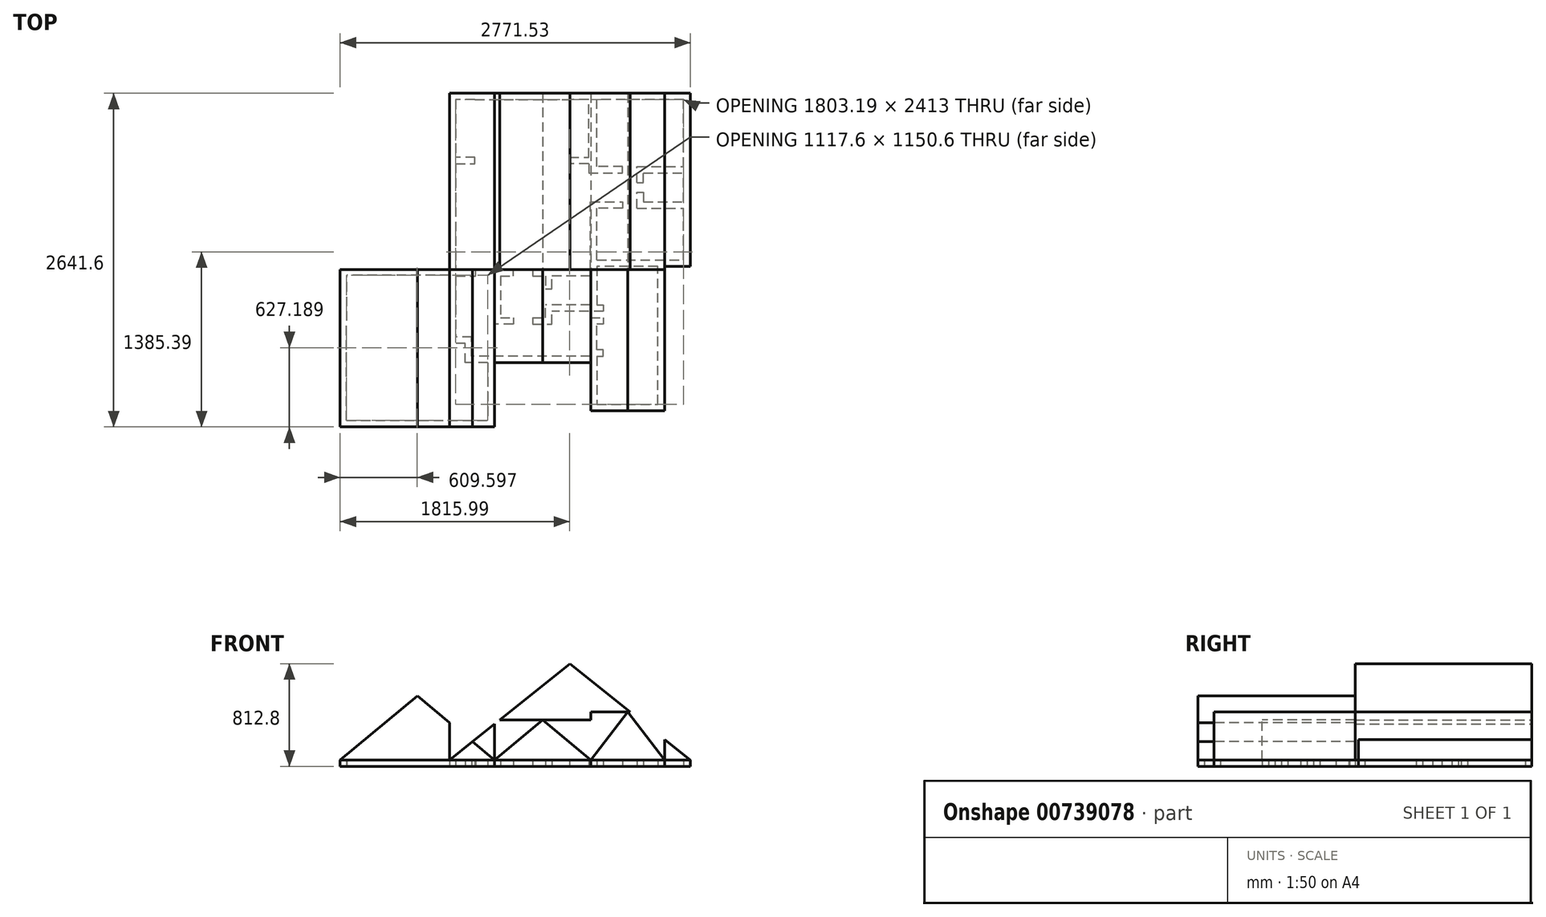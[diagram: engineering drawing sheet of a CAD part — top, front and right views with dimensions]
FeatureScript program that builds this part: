
annotation { "Feature Type Name" : "Feature", "Feature Type Description" : "" }
export const myFeature = defineFeature(function(context is Context, id is Id, definition is map)
    precondition{}
    {
        {
            var Q0;
            Q0=qCreatedBy(makeId("Top.planeOp"),FACE);
            var sketch = newSketch(context, id + "F0", { "sketchPlane" : qUnion([Q0])});
            skLineSegment(sketch, "E0", {"start": v(-1139.86, -1123.82) * mm, "end": v(-606.46, -1123.82) * mm});
            skLineSegment(sketch, "E1", {"start": v(256.93, -615.82) * mm, "end": v(256.93, -996.82) * mm});
            skLineSegment(sketch, "E2", {"start": v(256.93, -996.82) * mm, "end": v(739.53, -996.82) * mm});
            skLineSegment(sketch, "E3", {"start": v(688.73, 146.18) * mm, "end": v(942.73, 146.18) * mm});
            skLineSegment(sketch, "E4", {"start": v(942.73, 1416.18) * mm, "end": v(256.93, 1416.18) * mm});
            skLineSegment(sketch, "E5", {"start": v(-908.33, 26.78) * mm, "end": v(-1441.73, 26.78) * mm});
            skLineSegment(sketch, "E6", {"start": v(-1444.66, 68.9) * mm, "end": v(-962.06, 68.9) * mm});
            skLineSegment(sketch, "E7", {"start": v(-1187.73, -1175.7) * mm, "end": v(-552.73, -1175.7) * mm});
            skLineSegment(sketch, "E8", {"start": v(-552.73, -1175.7) * mm, "end": v(-552.73, -667.7) * mm});
            skLineSegment(sketch, "E9", {"start": v(-552.73, -667.7) * mm, "end": v(209.27, -667.7) * mm});
            skLineSegment(sketch, "E10", {"start": v(209.27, -667.7) * mm, "end": v(209.27, -1048.7) * mm});
            skLineSegment(sketch, "E11", {"start": v(209.27, -1048.7) * mm, "end": v(793.47, -1048.7) * mm});
            skLineSegment(sketch, "E12", {"start": v(996.67, 94.3) * mm, "end": v(996.67, 1465.9) * mm});
            skLineSegment(sketch, "E13", {"start": v(996.67, 1465.9) * mm, "end": v(209.27, 1465.9) * mm});
            skLineSegment(sketch, "E14", {"start": v(-606.46, -667.7) * mm, "end": v(-657.26, -667.7) * mm});
            skLineSegment(sketch, "E15", {"start": v(-657.26, -667.7) * mm, "end": v(-784.26, -667.7) * mm});
            skLineSegment(sketch, "E16", {"start": v(-784.26, -667.7) * mm, "end": v(-784.26, -515.3) * mm});
            skLineSegment(sketch, "E17", {"start": v(-784.26, -515.3) * mm, "end": v(-908.33, -515.3) * mm});
            skLineSegment(sketch, "E18", {"start": v(-908.33, -515.3) * mm, "end": v(-908.33, 26.78) * mm});
            skLineSegment(sketch, "E19", {"start": v(-860.46, 19.18) * mm, "end": v(-860.46, -463.42) * mm});
            skLineSegment(sketch, "E20", {"start": v(-733.46, -615.82) * mm, "end": v(-606.46, -615.82) * mm});
            skLineSegment(sketch, "E21", {"start": v(-962.06, 68.9) * mm, "end": v(-908.33, 68.9) * mm});
            skLineSegment(sketch, "E22", {"start": v(-908.33, 68.9) * mm, "end": v(-908.33, 957.9) * mm});
            skLineSegment(sketch, "E23", {"start": v(-606.46, -667.7) * mm, "end": v(-606.46, -1123.82) * mm});
            skLineSegment(sketch, "E24", {"start": v(688.73, 95.38) * mm, "end": v(256.93, 95.38) * mm});
            skLineSegment(sketch, "E25", {"start": v(793.47, -1048.7) * mm, "end": v(793.47, 94.3) * mm});
            skLineSegment(sketch, "E26", {"start": v(793.47, 94.3) * mm, "end": v(996.67, 94.3) * mm});
            skLineSegment(sketch, "E27", {"start": v(739.53, -996.82) * mm, "end": v(739.53, 95.38) * mm});
            skLineSegment(sketch, "E28", {"start": v(739.53, 95.38) * mm, "end": v(688.73, 95.38) * mm});
            skLineSegment(sketch, "E29", {"start": v(256.93, -615.82) * mm, "end": v(307.73, -615.82) * mm});
            skLineSegment(sketch, "E30", {"start": v(383.93, -615.82) * mm, "end": v(510.93, -615.82) * mm});
            skLineSegment(sketch, "E31", {"start": v(739.53, -615.82) * mm, "end": v(637.93, -615.82) * mm});
            skLineSegment(sketch, "E32", {"start": v(383.93, -615.82) * mm, "end": v(383.93, -526.92) * mm});
            skLineSegment(sketch, "E33", {"start": v(739.53, -312.49) * mm, "end": v(739.53, -374.51) * mm});
            skLineSegment(sketch, "E34", {"start": v(383.93, -209.42) * mm, "end": v(510.93, -209.42) * mm});
            skLineSegment(sketch, "E35", {"start": v(739.53, -209.42) * mm, "end": v(637.93, -209.42) * mm});
            skLineSegment(sketch, "E36", {"start": v(383.93, -526.92) * mm, "end": v(383.93, -473.07) * mm});
            skLineSegment(sketch, "E37", {"start": v(383.93, -312.49) * mm, "end": v(383.93, -366.33) * mm});
            skLineSegment(sketch, "E38", {"start": v(256.93, -158.62) * mm, "end": v(256.93, 95.38) * mm});
            skLineSegment(sketch, "E39", {"start": v(510.93, -209.42) * mm, "end": v(510.93, -234.82) * mm});
            skLineSegment(sketch, "E40", {"start": v(510.93, -234.82) * mm, "end": v(409.33, -234.82) * mm});
            skLineSegment(sketch, "E41", {"start": v(409.33, -234.82) * mm, "end": v(409.33, -285.62) * mm});
            skLineSegment(sketch, "E42", {"start": v(409.33, -285.62) * mm, "end": v(714.13, -285.62) * mm});
            skLineSegment(sketch, "E43", {"start": v(714.13, -285.62) * mm, "end": v(714.13, -234.82) * mm});
            skLineSegment(sketch, "E44", {"start": v(714.13, -234.82) * mm, "end": v(637.93, -234.82) * mm});
            skLineSegment(sketch, "E45", {"start": v(637.93, -234.82) * mm, "end": v(637.93, -209.42) * mm});
            skLineSegment(sketch, "E46", {"start": v(383.93, -366.33) * mm, "end": v(409.33, -366.33) * mm});
            skLineSegment(sketch, "E47", {"start": v(409.33, -366.33) * mm, "end": v(409.33, -312.49) * mm});
            skLineSegment(sketch, "E48", {"start": v(409.33, -312.49) * mm, "end": v(714.13, -312.49) * mm});
            skLineSegment(sketch, "E49", {"start": v(714.13, -312.49) * mm, "end": v(714.13, -501.51) * mm});
            skLineSegment(sketch, "E50", {"start": v(714.13, -501.51) * mm, "end": v(409.33, -501.51) * mm});
            skLineSegment(sketch, "E51", {"start": v(409.33, -501.51) * mm, "end": v(409.33, -473.07) * mm});
            skLineSegment(sketch, "E52", {"start": v(409.33, -473.07) * mm, "end": v(383.93, -473.07) * mm});
            skLineSegment(sketch, "E53", {"start": v(510.93, -615.82) * mm, "end": v(510.93, -590.42) * mm});
            skLineSegment(sketch, "E54", {"start": v(510.93, -590.42) * mm, "end": v(409.33, -590.42) * mm});
            skLineSegment(sketch, "E55", {"start": v(409.33, -590.42) * mm, "end": v(409.33, -526.92) * mm});
            skLineSegment(sketch, "E56", {"start": v(409.33, -526.92) * mm, "end": v(714.13, -526.92) * mm});
            skLineSegment(sketch, "E57", {"start": v(714.13, -526.92) * mm, "end": v(714.13, -590.42) * mm});
            skLineSegment(sketch, "E58", {"start": v(714.13, -590.42) * mm, "end": v(637.93, -590.42) * mm});
            skLineSegment(sketch, "E59", {"start": v(637.93, -590.42) * mm, "end": v(637.93, -615.82) * mm});
            skLineSegment(sketch, "E60", {"start": v(307.73, -615.82) * mm, "end": v(307.73, -565.02) * mm});
            skLineSegment(sketch, "E61", {"start": v(307.73, -565.02) * mm, "end": v(256.93, -565.02) * mm});
            skLineSegment(sketch, "E62", {"start": v(256.93, -565.02) * mm, "end": v(256.93, -361.82) * mm});
            skLineSegment(sketch, "E63", {"start": v(256.93, -158.62) * mm, "end": v(256.93, -209.42) * mm});
            skLineSegment(sketch, "E64", {"start": v(574.64, 554.2) * mm, "end": v(942.73, 554.2) * mm});
            skLineSegment(sketch, "E65", {"start": v(192.01, 908.18) * mm, "end": v(192.01, 833.6) * mm});
            skLineSegment(sketch, "E66", {"start": v(192.01, 833.6) * mm, "end": v(460.34, 833.6) * mm});
            skLineSegment(sketch, "E67", {"start": v(460.34, 833.6) * mm, "end": v(460.34, 884.4) * mm});
            skLineSegment(sketch, "E68", {"start": v(460.34, 884.4) * mm, "end": v(256.93, 884.4) * mm});
            skLineSegment(sketch, "E69", {"start": v(256.93, 884.4) * mm, "end": v(256.93, 1416.18) * mm});
            skLineSegment(sketch, "E70", {"start": v(574.64, 833.6) * mm, "end": v(574.64, 884.4) * mm});
            skLineSegment(sketch, "E71", {"start": v(574.64, 884.4) * mm, "end": v(942.73, 884.4) * mm});
            skLineSegment(sketch, "E72", {"start": v(942.73, 884.4) * mm, "end": v(942.73, 1416.18) * mm});
            skLineSegment(sketch, "E73", {"start": v(574.64, 554.2) * mm, "end": v(574.64, 605) * mm});
            skLineSegment(sketch, "E74", {"start": v(942.73, 605) * mm, "end": v(942.73, 833.6) * mm});
            skLineSegment(sketch, "E75", {"start": v(942.73, 146.18) * mm, "end": v(942.73, 554.2) * mm});
            skLineSegment(sketch, "E76", {"start": v(688.73, 146.18) * mm, "end": v(256.93, 146.18) * mm});
            skLineSegment(sketch, "E77", {"start": v(256.93, 146.18) * mm, "end": v(256.93, 554.2) * mm});
            skLineSegment(sketch, "E78", {"start": v(206.13, 450.98) * mm, "end": v(206.13, 605) * mm});
            skLineSegment(sketch, "E79", {"start": v(206.13, 605) * mm, "end": v(460.34, 605) * mm});
            skLineSegment(sketch, "E80", {"start": v(460.34, 605) * mm, "end": v(460.34, 554.2) * mm});
            skLineSegment(sketch, "E81", {"start": v(460.34, 554.2) * mm, "end": v(256.93, 554.2) * mm});
            skLineSegment(sketch, "E82", {"start": v(574.64, 833.6) * mm, "end": v(574.64, 757.4) * mm});
            skLineSegment(sketch, "E83", {"start": v(574.64, 605) * mm, "end": v(574.64, 681.2) * mm});
            skLineSegment(sketch, "E84", {"start": v(574.64, 681.2) * mm, "end": v(625.44, 681.2) * mm});
            skLineSegment(sketch, "E85", {"start": v(625.44, 681.2) * mm, "end": v(625.44, 605) * mm});
            skLineSegment(sketch, "E86", {"start": v(625.44, 605) * mm, "end": v(942.73, 605) * mm});
            skLineSegment(sketch, "E87", {"start": v(574.64, 757.4) * mm, "end": v(625.44, 757.4) * mm});
            skLineSegment(sketch, "E88", {"start": v(625.44, 757.4) * mm, "end": v(625.44, 833.6) * mm});
            skLineSegment(sketch, "E89", {"start": v(625.44, 833.6) * mm, "end": v(942.73, 833.6) * mm});
            skLineSegment(sketch, "E90", {"start": v(-1774.86, -615.82) * mm, "end": v(-1774.86, 68.9) * mm});
            skLineSegment(sketch, "E91", {"start": v(-1774.86, 68.9) * mm, "end": v(-1444.66, 68.9) * mm});
            skLineSegment(sketch, "E92", {"start": v(-1441.73, 26.78) * mm, "end": v(-1721.13, 26.78) * mm});
            skLineSegment(sketch, "E93", {"start": v(-1724.06, -565.02) * mm, "end": v(-1721.13, 26.78) * mm});
            skLineSegment(sketch, "E94", {"start": v(-1187.73, -1175.7) * mm, "end": v(-1774.86, -1175.7) * mm});
            skLineSegment(sketch, "E95", {"start": v(-1774.86, -1175.7) * mm, "end": v(-1774.86, -615.82) * mm});
            skLineSegment(sketch, "E96", {"start": v(-1139.86, -1123.82) * mm, "end": v(-1724.06, -1123.82) * mm});
            skLineSegment(sketch, "E97", {"start": v(-1724.06, -1123.82) * mm, "end": v(-1724.06, -565.02) * mm});
            skLineSegment(sketch, "E98", {"start": v(192.01, 908.18) * mm, "end": v(39.61, 908.18) * mm});
            skLineSegment(sketch, "E99", {"start": v(39.61, 908.18) * mm, "end": v(39.61, 957.9) * mm});
            skLineSegment(sketch, "E100", {"start": v(-860.46, 908.18) * mm, "end": v(-708.06, 908.18) * mm});
            skLineSegment(sketch, "E101", {"start": v(-708.06, 908.18) * mm, "end": v(-708.06, 957.9) * mm});
            skLineSegment(sketch, "E102", {"start": v(-708.06, 957.9) * mm, "end": v(-860.46, 957.9) * mm});
            skLineSegment(sketch, "E103", {"start": v(39.61, 957.9) * mm, "end": v(192.01, 957.9) * mm});
            skLineSegment(sketch, "E104", {"start": v(192.01, 957.9) * mm, "end": v(192.01, 1416.18) * mm});
            skLineSegment(sketch, "E105", {"start": v(192.01, 1416.18) * mm, "end": v(39.61, 1416.18) * mm});
            skLineSegment(sketch, "E106", {"start": v(39.61, 1465.9) * mm, "end": v(209.27, 1465.9) * mm});
            skLineSegment(sketch, "E107", {"start": v(-908.33, 957.9) * mm, "end": v(-908.33, 1465.9) * mm});
            skLineSegment(sketch, "E108", {"start": v(-908.33, 1465.9) * mm, "end": v(-708.06, 1465.9) * mm});
            skLineSegment(sketch, "E109", {"start": v(-708.06, 1415.1) * mm, "end": v(-860.46, 1415.1) * mm});
            skLineSegment(sketch, "E110", {"start": v(-860.46, 1415.1) * mm, "end": v(-860.46, 957.9) * mm});
            skLineSegment(sketch, "E111", {"start": v(206.13, -361.82) * mm, "end": v(206.13, -615.82) * mm});
            skLineSegment(sketch, "E112", {"start": v(206.13, -615.82) * mm, "end": v(-606.46, -615.82) * mm});
            skLineSegment(sketch, "E113", {"start": v(206.13, -260.22) * mm, "end": v(256.93, -260.22) * mm});
            skLineSegment(sketch, "E114", {"start": v(383.93, -312.49) * mm, "end": v(383.93, -260.22) * mm});
            skLineSegment(sketch, "E115", {"start": v(383.93, -260.22) * mm, "end": v(383.93, -209.42) * mm});
            skLineSegment(sketch, "E116", {"start": v(256.93, -209.42) * mm, "end": v(307.73, -209.42) * mm});
            skLineSegment(sketch, "E117", {"start": v(307.73, -209.42) * mm, "end": v(307.73, -260.22) * mm});
            skLineSegment(sketch, "E118", {"start": v(307.73, -260.22) * mm, "end": v(256.93, -260.22) * mm});
            skLineSegment(sketch, "E119", {"start": v(-733.46, -615.82) * mm, "end": v(-733.46, -463.42) * mm});
            skLineSegment(sketch, "E120", {"start": v(-733.46, -463.42) * mm, "end": v(-860.46, -463.42) * mm});
            skLineSegment(sketch, "E121", {"start": v(256.93, -311.02) * mm, "end": v(307.73, -311.02) * mm});
            skLineSegment(sketch, "E122", {"start": v(307.73, -311.02) * mm, "end": v(307.73, -361.82) * mm});
            skLineSegment(sketch, "E123", {"start": v(307.73, -361.82) * mm, "end": v(256.93, -361.82) * mm});
            skLineSegment(sketch, "E124", {"start": v(-708.06, 1415.1) * mm, "end": v(39.61, 1416.18) * mm});
            skLineSegment(sketch, "E125", {"start": v(39.61, 1465.9) * mm, "end": v(-708.06, 1465.9) * mm});
            skLineSegment(sketch, "E126", {"start": v(206.13, -311.02) * mm, "end": v(256.93, -311.02) * mm});
            skLineSegment(sketch, "E127", {"start": v(206.13, -615.82) * mm, "end": v(-98.67, -615.82) * mm});
            skLineSegment(sketch, "E128", {"start": v(-252.28, -311.02) * mm, "end": v(-252.28, -361.82) * mm});
            skLineSegment(sketch, "E129", {"start": v(-252.28, -311.02) * mm, "end": v(-201.48, -311.02) * mm});
            skLineSegment(sketch, "E130", {"start": v(206.13, 450.98) * mm, "end": v(206.13, 196.98) * mm});
            skLineSegment(sketch, "E131", {"start": v(-252.28, -361.82) * mm, "end": v(-99.88, -361.82) * mm});
            skLineSegment(sketch, "E132", {"start": v(-99.88, -361.82) * mm, "end": v(-99.88, -311.02) * mm});
            skLineSegment(sketch, "E133", {"start": v(206.13, 196.98) * mm, "end": v(206.13, 146.18) * mm});
            skLineSegment(sketch, "E134", {"start": v(-404.68, -361.82) * mm, "end": v(-557.08, -361.82) * mm});
            skLineSegment(sketch, "E135", {"start": v(-557.08, -361.82) * mm, "end": v(-557.08, -311.02) * mm});
            skLineSegment(sketch, "E136", {"start": v(-404.68, -311.02) * mm, "end": v(-404.68, -361.82) * mm});
            skLineSegment(sketch, "E137", {"start": v(-860.46, 19.18) * mm, "end": v(-702.13, 19.18) * mm});
            skLineSegment(sketch, "E138", {"start": v(-404.68, 19.18) * mm, "end": v(-404.68, 69.98) * mm});
            skLineSegment(sketch, "E139", {"start": v(-404.68, 69.98) * mm, "end": v(-557.08, 69.98) * mm});
            skLineSegment(sketch, "E140", {"start": v(-557.08, 69.98) * mm, "end": v(-557.08, 19.18) * mm});
            skLineSegment(sketch, "E141", {"start": v(-702.13, 19.18) * mm, "end": v(-702.13, 69.98) * mm});
            skLineSegment(sketch, "E142", {"start": v(-702.13, 69.98) * mm, "end": v(-860.46, 69.98) * mm});
            skLineSegment(sketch, "E143", {"start": v(-201.48, -311.02) * mm, "end": v(-150.68, -311.02) * mm});
            skLineSegment(sketch, "E144", {"start": v(-557.08, -311.02) * mm, "end": v(-557.08, 19.18) * mm});
            skLineSegment(sketch, "E145", {"start": v(-506.28, 19.18) * mm, "end": v(-506.28, -311.02) * mm});
            skLineSegment(sketch, "E146", {"start": v(-99.88, 69.98) * mm, "end": v(-252.28, 69.98) * mm});
            skLineSegment(sketch, "E147", {"start": v(-252.28, 69.98) * mm, "end": v(-252.28, 19.18) * mm});
            skLineSegment(sketch, "E148", {"start": v(-252.28, 19.18) * mm, "end": v(-150.68, 19.18) * mm});
            skLineSegment(sketch, "E149", {"start": v(-506.28, 19.18) * mm, "end": v(-404.68, 19.18) * mm});
            skLineSegment(sketch, "E150", {"start": v(-506.28, -311.02) * mm, "end": v(-404.68, -311.02) * mm});
            skLineSegment(sketch, "E151", {"start": v(-860.46, 908.18) * mm, "end": v(-860.46, 69.98) * mm});
            skLineSegment(sketch, "E152", {"start": v(206.13, 69.98) * mm, "end": v(53.73, 69.98) * mm});
            skPoint(sketch, "E152.startSnap0", {"position": v(-176.08, 69.98) * mm});
            skPoint(sketch, "E152.endSnap0", {"position": v(-781.3, 69.98) * mm});
            skLineSegment(sketch, "E153", {"start": v(53.73, 19.18) * mm, "end": v(206.13, 19.18) * mm});
            skLineSegment(sketch, "E154", {"start": v(206.13, 69.98) * mm, "end": v(206.13, 146.18) * mm});
            skLineSegment(sketch, "E155", {"start": v(206.13, -361.82) * mm, "end": v(206.13, -311.02) * mm});
            skLineSegment(sketch, "E156", {"start": v(-99.88, 69.98) * mm, "end": v(53.73, 69.98) * mm});
            skLineSegment(sketch, "E157", {"start": v(53.73, 19.18) * mm, "end": v(-99.88, 19.18) * mm});
            skLineSegment(sketch, "E158", {"start": v(-99.88, -260.22) * mm, "end": v(-99.88, -311.02) * mm});
            skLineSegment(sketch, "E159", {"start": v(206.13, -184.02) * mm, "end": v(206.13, -6.21) * mm});
            skLineSegment(sketch, "E160", {"start": v(206.13, -6.21) * mm, "end": v(206.13, 19.18) * mm});
            skLineSegment(sketch, "E161", {"start": v(206.13, -209.42) * mm, "end": v(206.13, -184.02) * mm});
            skLineSegment(sketch, "E162", {"start": v(206.13, -260.22) * mm, "end": v(-99.88, -260.22) * mm});
            skLineSegment(sketch, "E163", {"start": v(206.13, -209.42) * mm, "end": v(-99.88, -209.42) * mm});
            skLineSegment(sketch, "E164", {"start": v(-150.68, -209.42) * mm, "end": v(-99.88, -209.42) * mm});
            skLineSegment(sketch, "E165", {"start": v(-150.68, -311.02) * mm, "end": v(-150.68, -209.42) * mm});
            skLineSegment(sketch, "E166", {"start": v(-150.68, 19.18) * mm, "end": v(-150.68, -82.42) * mm});
            skLineSegment(sketch, "E167", {"start": v(-150.68, -82.42) * mm, "end": v(-99.88, -82.42) * mm});
            skLineSegment(sketch, "E168", {"start": v(-99.88, -82.42) * mm, "end": v(-99.88, 19.18) * mm});
            skSolve(sketch);
        }
        {
            var Q0;
            Q0 = qSketchRegion(id + "F0", true);
            var Q1;
            Q1=makeQuery(id+"F0.imprint","IMPRINT",FACE,{"disambiguationData":[TD([[makeQuery(id+"F0.imprint","IMPRINT",EDGE,{"derivedFrom":sQuery(id+"F0.wireOp",EDGE,"E134")}),-1.0]])]});
            extrude(context, id + "F1", {"entities" : qUnion([Q0, Q1]), "depth" : 50.8 * mm, "offsetDistance" : 25.4 * mm});
        }
        {
            var Q0;
            Q0=makeQuery(id+"F1.opExtrude","CAP_FACE",FACE,{"disambiguationData":[OSD([sQuery(id+"F0.wireOp",EDGE,"E0"),sQuery(id+"F0.wireOp",EDGE,"E1"),sQuery(id+"F0.wireOp",EDGE,"E2"),sQuery(id+"F0.wireOp",EDGE,"E3"),sQuery(id+"F0.wireOp",EDGE,"E4"),sQuery(id+"F0.wireOp",EDGE,"E5"),sQuery(id+"F0.wireOp",EDGE,"E6"),sQuery(id+"F0.wireOp",EDGE,"E7"),sQuery(id+"F0.wireOp",EDGE,"E8"),sQuery(id+"F0.wireOp",EDGE,"E9"),sQuery(id+"F0.wireOp",EDGE,"E10"),sQuery(id+"F0.wireOp",EDGE,"E11"),sQuery(id+"F0.wireOp",EDGE,"E12"),sQuery(id+"F0.wireOp",EDGE,"E13"),sQuery(id+"F0.wireOp",EDGE,"E14"),sQuery(id+"F0.wireOp",EDGE,"E15"),sQuery(id+"F0.wireOp",EDGE,"E16"),sQuery(id+"F0.wireOp",EDGE,"E17"),sQuery(id+"F0.wireOp",EDGE,"E18"),sQuery(id+"F0.wireOp",EDGE,"E19"),sQuery(id+"F0.wireOp",EDGE,"E20"),sQuery(id+"F0.wireOp",EDGE,"E21"),sQuery(id+"F0.wireOp",EDGE,"E22"),sQuery(id+"F0.wireOp",EDGE,"E23"),sQuery(id+"F0.wireOp",EDGE,"E24"),sQuery(id+"F0.wireOp",EDGE,"E25"),sQuery(id+"F0.wireOp",EDGE,"E26"),sQuery(id+"F0.wireOp",EDGE,"E27"),sQuery(id+"F0.wireOp",EDGE,"E28"),sQuery(id+"F0.wireOp",EDGE,"E29"),sQuery(id+"F0.wireOp",EDGE,"E33"),sQuery(id+"F0.wireOp",EDGE,"E38"),sQuery(id+"F0.wireOp",EDGE,"E60"),sQuery(id+"F0.wireOp",EDGE,"E61"),sQuery(id+"F0.wireOp",EDGE,"E62"),sQuery(id+"F0.wireOp",EDGE,"E63"),sQuery(id+"F0.wireOp",EDGE,"E64"),sQuery(id+"F0.wireOp",EDGE,"E65"),sQuery(id+"F0.wireOp",EDGE,"E66"),sQuery(id+"F0.wireOp",EDGE,"E67"),sQuery(id+"F0.wireOp",EDGE,"E68"),sQuery(id+"F0.wireOp",EDGE,"E69"),sQuery(id+"F0.wireOp",EDGE,"E70"),sQuery(id+"F0.wireOp",EDGE,"E71"),sQuery(id+"F0.wireOp",EDGE,"E72"),sQuery(id+"F0.wireOp",EDGE,"E73"),sQuery(id+"F0.wireOp",EDGE,"E74"),sQuery(id+"F0.wireOp",EDGE,"E75"),sQuery(id+"F0.wireOp",EDGE,"E76"),sQuery(id+"F0.wireOp",EDGE,"E77"),sQuery(id+"F0.wireOp",EDGE,"E78"),sQuery(id+"F0.wireOp",EDGE,"E79"),sQuery(id+"F0.wireOp",EDGE,"E80"),sQuery(id+"F0.wireOp",EDGE,"E81"),sQuery(id+"F0.wireOp",EDGE,"E82"),sQuery(id+"F0.wireOp",EDGE,"E83"),sQuery(id+"F0.wireOp",EDGE,"E84"),sQuery(id+"F0.wireOp",EDGE,"E85"),sQuery(id+"F0.wireOp",EDGE,"E86"),sQuery(id+"F0.wireOp",EDGE,"E87"),sQuery(id+"F0.wireOp",EDGE,"E88"),sQuery(id+"F0.wireOp",EDGE,"E89"),sQuery(id+"F0.wireOp",EDGE,"E90"),sQuery(id+"F0.wireOp",EDGE,"E91"),sQuery(id+"F0.wireOp",EDGE,"E92"),sQuery(id+"F0.wireOp",EDGE,"E93"),sQuery(id+"F0.wireOp",EDGE,"E94"),sQuery(id+"F0.wireOp",EDGE,"E95"),sQuery(id+"F0.wireOp",EDGE,"E96"),sQuery(id+"F0.wireOp",EDGE,"E97"),sQuery(id+"F0.wireOp",EDGE,"E98"),sQuery(id+"F0.wireOp",EDGE,"E99"),sQuery(id+"F0.wireOp",EDGE,"E100"),sQuery(id+"F0.wireOp",EDGE,"E101"),sQuery(id+"F0.wireOp",EDGE,"E102"),sQuery(id+"F0.wireOp",EDGE,"E103"),sQuery(id+"F0.wireOp",EDGE,"E104"),sQuery(id+"F0.wireOp",EDGE,"E105"),sQuery(id+"F0.wireOp",EDGE,"E106"),sQuery(id+"F0.wireOp",EDGE,"E107"),sQuery(id+"F0.wireOp",EDGE,"E108"),sQuery(id+"F0.wireOp",EDGE,"E109"),sQuery(id+"F0.wireOp",EDGE,"E110"),sQuery(id+"F0.wireOp",EDGE,"E111"),sQuery(id+"F0.wireOp",EDGE,"E112"),sQuery(id+"F0.wireOp",EDGE,"E113"),sQuery(id+"F0.wireOp",EDGE,"E116"),sQuery(id+"F0.wireOp",EDGE,"E117"),sQuery(id+"F0.wireOp",EDGE,"E118"),sQuery(id+"F0.wireOp",EDGE,"E119"),sQuery(id+"F0.wireOp",EDGE,"E120"),sQuery(id+"F0.wireOp",EDGE,"E121"),sQuery(id+"F0.wireOp",EDGE,"E122"),sQuery(id+"F0.wireOp",EDGE,"E123"),sQuery(id+"F0.wireOp",EDGE,"E124"),sQuery(id+"F0.wireOp",EDGE,"E125"),sQuery(id+"F0.wireOp",EDGE,"E126"),sQuery(id+"F0.wireOp",EDGE,"E127"),sQuery(id+"F0.wireOp",EDGE,"E128"),sQuery(id+"F0.wireOp",EDGE,"E129"),sQuery(id+"F0.wireOp",EDGE,"E130"),sQuery(id+"F0.wireOp",EDGE,"E131"),sQuery(id+"F0.wireOp",EDGE,"E132"),sQuery(id+"F0.wireOp",EDGE,"E133"),sQuery(id+"F0.wireOp",EDGE,"E137"),sQuery(id+"F0.wireOp",EDGE,"E141"),sQuery(id+"F0.wireOp",EDGE,"E142"),sQuery(id+"F0.wireOp",EDGE,"E143"),sQuery(id+"F0.wireOp",EDGE,"E146"),sQuery(id+"F0.wireOp",EDGE,"E147"),sQuery(id+"F0.wireOp",EDGE,"E148"),sQuery(id+"F0.wireOp",EDGE,"E151"),sQuery(id+"F0.wireOp",EDGE,"E152"),sQuery(id+"F0.wireOp",EDGE,"E153"),sQuery(id+"F0.wireOp",EDGE,"E154"),sQuery(id+"F0.wireOp",EDGE,"E155"),sQuery(id+"F0.wireOp",EDGE,"E156"),sQuery(id+"F0.wireOp",EDGE,"E157"),sQuery(id+"F0.wireOp",EDGE,"E158"),sQuery(id+"F0.wireOp",EDGE,"E159"),sQuery(id+"F0.wireOp",EDGE,"E160"),sQuery(id+"F0.wireOp",EDGE,"E161"),sQuery(id+"F0.wireOp",EDGE,"E162"),sQuery(id+"F0.wireOp",EDGE,"E163"),sQuery(id+"F0.wireOp",EDGE,"E164"),sQuery(id+"F0.wireOp",EDGE,"E165"),sQuery(id+"F0.wireOp",EDGE,"E166"),sQuery(id+"F0.wireOp",EDGE,"E167"),sQuery(id+"F0.wireOp",EDGE,"E168")])],"isStart":true});
            var sketch = newSketch(context, id + "F2", { "sketchPlane" : qUnion([Q0])});
            skLineSegment(sketch, "E169", {"start": v(-1774.86, 1175.7) * mm, "end": v(-1774.86, -68.9) * mm});
            skLineSegment(sketch, "E170", {"start": v(-1774.86, -68.9) * mm, "end": v(-908.33, -68.9) * mm});
            skLineSegment(sketch, "E171", {"start": v(-908.33, -68.9) * mm, "end": v(-908.33, -1465.9) * mm});
            skLineSegment(sketch, "E172", {"start": v(-908.33, -1465.9) * mm, "end": v(996.67, -1465.9) * mm});
            skLineSegment(sketch, "E173", {"start": v(996.67, -1465.9) * mm, "end": v(996.67, -94.3) * mm});
            skLineSegment(sketch, "E174", {"start": v(996.67, -94.3) * mm, "end": v(793.47, -94.3) * mm});
            skLineSegment(sketch, "E175", {"start": v(793.47, -94.3) * mm, "end": v(793.47, 1048.7) * mm});
            skLineSegment(sketch, "E176", {"start": v(793.47, 1048.7) * mm, "end": v(209.27, 1048.7) * mm});
            skLineSegment(sketch, "E177", {"start": v(209.27, 1048.7) * mm, "end": v(209.27, 667.7) * mm});
            skLineSegment(sketch, "E178", {"start": v(209.27, 667.7) * mm, "end": v(-552.73, 667.7) * mm});
            skLineSegment(sketch, "E179", {"start": v(-552.73, 667.7) * mm, "end": v(-552.73, 1175.7) * mm});
            skLineSegment(sketch, "E180", {"start": v(-552.73, 1175.7) * mm, "end": v(-1774.86, 1175.7) * mm});
            skSolve(sketch);
        }
        {
            var Q0;
            Q0 = qSketchRegion(id + "F2", true);
            extrude(context, id + "F3", {"entities" : qUnion([Q0]), "oppositeDirection" : true, "depth" : 50.8 * mm, "offsetDistance" : 25.4 * mm});
        }
        {
            var Q0;
            Q0=makeQuery(id+"F3.opExtrude","CAP_FACE",FACE,{"disambiguationData":[OSD([sQuery(id+"F2.wireOp",EDGE,"E169"),sQuery(id+"F2.wireOp",EDGE,"E170"),sQuery(id+"F2.wireOp",EDGE,"E171"),sQuery(id+"F2.wireOp",EDGE,"E172"),sQuery(id+"F2.wireOp",EDGE,"E173"),sQuery(id+"F2.wireOp",EDGE,"E174"),sQuery(id+"F2.wireOp",EDGE,"E175"),sQuery(id+"F2.wireOp",EDGE,"E176"),sQuery(id+"F2.wireOp",EDGE,"E177"),sQuery(id+"F2.wireOp",EDGE,"E178"),sQuery(id+"F2.wireOp",EDGE,"E179"),sQuery(id+"F2.wireOp",EDGE,"E180")])],"isStart":false});
            var sketch = newSketch(context, id + "F4", { "sketchPlane" : qUnion([Q0])});
            skLineSegment(sketch, "E181", {"start": v(-1774.86, -1175.7) * mm, "end": v(-552.73, -1175.7) * mm});
            skLineSegment(sketch, "E182", {"start": v(-552.73, -1175.7) * mm, "end": v(-552.73, 68.9) * mm});
            skLineSegment(sketch, "E183", {"start": v(-552.73, 68.9) * mm, "end": v(-1774.86, 68.9) * mm});
            skLineSegment(sketch, "E184", {"start": v(-1774.86, 68.9) * mm, "end": v(-1774.86, -1175.7) * mm});
            skLineSegment(sketch, "E185", {"start": v(209.27, -1048.7) * mm, "end": v(209.27, 94.3) * mm});
            skLineSegment(sketch, "E186", {"start": v(209.27, 94.3) * mm, "end": v(793.47, 94.3) * mm});
            skLineSegment(sketch, "E187", {"start": v(793.47, 94.3) * mm, "end": v(793.47, -1048.7) * mm});
            skLineSegment(sketch, "E188", {"start": v(793.47, -1048.7) * mm, "end": v(209.27, -1048.7) * mm});
            skLineSegment(sketch, "E189", {"start": v(209.27, 94.3) * mm, "end": v(-908.33, 94.3) * mm});
            skLineSegment(sketch, "E190", {"start": v(-908.33, 94.3) * mm, "end": v(-908.33, 68.9) * mm});
            skSolve(sketch);
        }
        {
            var Q0;
            {var subQ6=sQuery(id+"F4.wireOp",EDGE,"E181");Q0=makeQuery(id+"F4.imprint","IMPRINT",FACE,{"disambiguationData":[TD([[makeQuery(id+"F4.imprint","IMPRINT",EDGE,{"derivedFrom":subQ6}),-1.0]])]});}
            extrude(context, id + "F5", {"entities" : qUnion([Q0]), "depth" : 508 * mm, "offsetDistance" : 25.4 * mm});
        }
        {
            var Q0;
            Q0=makeQuery(id+"F5.opExtrude","SWEPT_FACE",FACE,{"disambiguationData":[OSD([sQuery(id+"F4.wireOp",EDGE,"E181")])]});
            var sketch = newSketch(context, id + "F6", { "sketchPlane" : qUnion([Q0])});
            skLineSegment(sketch, "E191", {"start": v(-1774.86, 50.8) * mm, "end": v(-1163.8, 558.8) * mm});
            skLineSegment(sketch, "E192", {"start": v(-1163.8, 558.8) * mm, "end": v(-552.73, 50.8) * mm});
            skSolve(sketch);
        }
        {
            var Q0;
            {var subQ0=sQuery(id+"F6.wireOp",EDGE,"E191");Q0=makeQuery(id+"F6.imprint","IMPRINT",FACE,{"disambiguationData":[TD([[makeQuery(id+"F6.imprint","IMPRINT",EDGE,{"derivedFrom":subQ0}),1.0]])]});}
            var Q1;
            {var subQ0=sQuery(id+"F6.wireOp",EDGE,"E192");Q1=makeQuery(id+"F6.imprint","IMPRINT",FACE,{"disambiguationData":[TD([[makeQuery(id+"F6.imprint","IMPRINT",EDGE,{"derivedFrom":subQ0}),1.0]])]});}
            extrude(context, id + "F7", {"entities" : qUnion([Q0, Q1]), "operationType" : NewBodyOperationType.REMOVE, "endBound" : BoundingType.THROUGH_ALL, "oppositeDirection" : true, "depth" : 25.4 * mm, "offsetDistance" : 25.4 * mm});
        }
        {
            var Q0;
            Q0=makeQuery(id+"F3.opExtrude","CAP_FACE",FACE,{"disambiguationData":[OSD([sQuery(id+"F2.wireOp",EDGE,"E169"),sQuery(id+"F2.wireOp",EDGE,"E170"),sQuery(id+"F2.wireOp",EDGE,"E171"),sQuery(id+"F2.wireOp",EDGE,"E172"),sQuery(id+"F2.wireOp",EDGE,"E173"),sQuery(id+"F2.wireOp",EDGE,"E174"),sQuery(id+"F2.wireOp",EDGE,"E175"),sQuery(id+"F2.wireOp",EDGE,"E176"),sQuery(id+"F2.wireOp",EDGE,"E177"),sQuery(id+"F2.wireOp",EDGE,"E178"),sQuery(id+"F2.wireOp",EDGE,"E179"),sQuery(id+"F2.wireOp",EDGE,"E180")])],"isStart":false});
            var sketch = newSketch(context, id + "F8", { "sketchPlane" : qUnion([Q0])});
            skLineSegment(sketch, "E193", {"start": v(-908.33, 68.9) * mm, "end": v(793.47, 68.9) * mm});
            skLineSegment(sketch, "E194", {"start": v(793.47, 68.9) * mm, "end": v(793.47, 94.3) * mm});
            skLineSegment(sketch, "E195", {"start": v(793.47, 94.3) * mm, "end": v(996.67, 94.3) * mm});
            skLineSegment(sketch, "E196", {"start": v(996.67, 94.3) * mm, "end": v(996.67, 1465.9) * mm});
            skLineSegment(sketch, "E197", {"start": v(996.67, 1465.9) * mm, "end": v(-908.33, 1465.9) * mm});
            skLineSegment(sketch, "E198", {"start": v(-908.33, 1465.9) * mm, "end": v(-908.33, 68.9) * mm});
            skSolve(sketch);
        }
        {
            var Q0;
            Q0 = qSketchRegion(id + "F8", true);
            extrude(context, id + "F9", {"entities" : qUnion([Q0]), "depth" : 762 * mm, "offsetDistance" : 25.4 * mm});
        }
        {
            var Q0;
            Q0=makeQuery(id+"F9.opExtrude","SWEPT_FACE",FACE,{"disambiguationData":[OSD([sQuery(id+"F8.wireOp",EDGE,"E197")])]});
            var sketch = newSketch(context, id + "F10", { "sketchPlane" : qUnion([Q0])});
            skLineSegment(sketch, "E199", {"start": v(-996.67, 50.8) * mm, "end": v(-44.17, 812.8) * mm});
            skLineSegment(sketch, "E200", {"start": v(-44.17, 812.8) * mm, "end": v(908.33, 50.8) * mm});
            skLineSegment(sketch, "E201", {"start": v(908.33, 50.8) * mm, "end": v(-996.67, 50.8) * mm});
            skSolve(sketch);
        }
        {
            var Q0;
            {var subQ0=sQuery(id+"F10.wireOp",EDGE,"E199");Q0=makeQuery(id+"F10.imprint","IMPRINT",FACE,{"disambiguationData":[TD([[makeQuery(id+"F10.imprint","IMPRINT",EDGE,{"derivedFrom":subQ0}),1.0]])]});}
            var Q1;
            {var subQ0=sQuery(id+"F10.wireOp",EDGE,"E200");Q1=makeQuery(id+"F10.imprint","IMPRINT",FACE,{"disambiguationData":[TD([[makeQuery(id+"F10.imprint","IMPRINT",EDGE,{"derivedFrom":subQ0}),1.0]])]});}
            extrude(context, id + "F11", {"entities" : qUnion([Q0, Q1]), "operationType" : NewBodyOperationType.REMOVE, "endBound" : BoundingType.THROUGH_ALL, "oppositeDirection" : true, "depth" : 25.4 * mm, "offsetDistance" : 25.4 * mm});
        }
        {
            var Q0;
            Q0=makeQuery(id+"F3.opExtrude","CAP_FACE",FACE,{"disambiguationData":[OSD([sQuery(id+"F2.wireOp",EDGE,"E169"),sQuery(id+"F2.wireOp",EDGE,"E170"),sQuery(id+"F2.wireOp",EDGE,"E171"),sQuery(id+"F2.wireOp",EDGE,"E172"),sQuery(id+"F2.wireOp",EDGE,"E173"),sQuery(id+"F2.wireOp",EDGE,"E174"),sQuery(id+"F2.wireOp",EDGE,"E175"),sQuery(id+"F2.wireOp",EDGE,"E176"),sQuery(id+"F2.wireOp",EDGE,"E177"),sQuery(id+"F2.wireOp",EDGE,"E178"),sQuery(id+"F2.wireOp",EDGE,"E179"),sQuery(id+"F2.wireOp",EDGE,"E180")])],"isStart":false});
            var sketch = newSketch(context, id + "F12", { "sketchPlane" : qUnion([Q0])});
            skLineSegment(sketch, "E202", {"start": v(209.27, -1048.7) * mm, "end": v(209.27, 68.9) * mm});
            skLineSegment(sketch, "E203", {"start": v(209.27, 68.9) * mm, "end": v(793.47, 68.9) * mm});
            skLineSegment(sketch, "E204", {"start": v(793.47, 68.9) * mm, "end": v(793.47, -1048.7) * mm});
            skLineSegment(sketch, "E205", {"start": v(793.47, -1048.7) * mm, "end": v(209.27, -1048.7) * mm});
            skSolve(sketch);
        }
        {
            var Q0;
            Q0 = qSketchRegion(id + "F12", true);
            extrude(context, id + "F13", {"entities" : qUnion([Q0]), "depth" : 381 * mm, "offsetDistance" : 25.4 * mm});
        }
        {
            var Q0;
            Q0=makeQuery(id+"F13.opExtrude","SWEPT_FACE",FACE,{"disambiguationData":[OSD([sQuery(id+"F12.wireOp",EDGE,"E205")])]});
            var sketch = newSketch(context, id + "F14", { "sketchPlane" : qUnion([Q0])});
            skLineSegment(sketch, "E206", {"start": v(209.27, 50.8) * mm, "end": v(501.37, 431.8) * mm});
            skLineSegment(sketch, "E207", {"start": v(501.37, 431.8) * mm, "end": v(793.47, 50.8) * mm});
            skSolve(sketch);
        }
        {
            var Q0;
            {var subQ0=sQuery(id+"F14.wireOp",EDGE,"E206");Q0=makeQuery(id+"F14.imprint","IMPRINT",FACE,{"disambiguationData":[TD([[makeQuery(id+"F14.imprint","IMPRINT",EDGE,{"derivedFrom":subQ0}),1.0]])]});}
            var Q1;
            {var subQ0=sQuery(id+"F14.wireOp",EDGE,"E207");Q1=makeQuery(id+"F14.imprint","IMPRINT",FACE,{"disambiguationData":[TD([[makeQuery(id+"F14.imprint","IMPRINT",EDGE,{"derivedFrom":subQ0}),1.0]])]});}
            extrude(context, id + "F15", {"entities" : qUnion([Q0, Q1]), "operationType" : NewBodyOperationType.REMOVE, "endBound" : BoundingType.THROUGH_ALL, "oppositeDirection" : true, "depth" : 25.4 * mm, "offsetDistance" : 25.4 * mm});
        }
        {
            var Q0;
            Q0=makeQuery(id+"F3.opExtrude","CAP_FACE",FACE,{"disambiguationData":[OSD([sQuery(id+"F2.wireOp",EDGE,"E169"),sQuery(id+"F2.wireOp",EDGE,"E170"),sQuery(id+"F2.wireOp",EDGE,"E171"),sQuery(id+"F2.wireOp",EDGE,"E172"),sQuery(id+"F2.wireOp",EDGE,"E173"),sQuery(id+"F2.wireOp",EDGE,"E174"),sQuery(id+"F2.wireOp",EDGE,"E175"),sQuery(id+"F2.wireOp",EDGE,"E176"),sQuery(id+"F2.wireOp",EDGE,"E177"),sQuery(id+"F2.wireOp",EDGE,"E178"),sQuery(id+"F2.wireOp",EDGE,"E179"),sQuery(id+"F2.wireOp",EDGE,"E180")])],"isStart":false});
            var sketch = newSketch(context, id + "F16", { "sketchPlane" : qUnion([Q0])});
            skLineSegment(sketch, "E208", {"start": v(-552.73, -667.7) * mm, "end": v(209.27, -667.7) * mm});
            skLineSegment(sketch, "E209.0", {"start": v(44.17, 68.9) * mm, "end": v(-908.33, 68.9) * mm});
            skLineSegment(sketch, "E210.0", {"start": v(793.47, 68.9) * mm, "end": v(44.17, 68.9) * mm});
            skLineSegment(sketch, "E211", {"start": v(209.27, -667.7) * mm, "end": v(209.27, 68.9) * mm});
            skLineSegment(sketch, "E212", {"start": v(209.27, 68.9) * mm, "end": v(-552.73, 68.9) * mm});
            skLineSegment(sketch, "E213", {"start": v(-552.73, 68.9) * mm, "end": v(-552.73, -667.7) * mm});
            skSolve(sketch);
        }
        {
            var Q0;
            Q0 = qSketchRegion(id + "F16", true);
            extrude(context, id + "F17", {"entities" : qUnion([Q0]), "depth" : 317.5 * mm, "offsetDistance" : 25.4 * mm});
        }
        {
            var Q0;
            Q0=makeQuery(id+"F17.opExtrude","SWEPT_FACE",FACE,{"disambiguationData":[OSD([sQuery(id+"F16.wireOp",EDGE,"E208")])]});
            var sketch = newSketch(context, id + "F18", { "sketchPlane" : qUnion([Q0])});
            skLineSegment(sketch, "E214", {"start": v(-552.73, 50.8) * mm, "end": v(-171.73, 368.3) * mm});
            skLineSegment(sketch, "E215", {"start": v(-171.73, 368.3) * mm, "end": v(209.27, 50.8) * mm});
            skSolve(sketch);
        }
        {
            var Q0;
            {var subQ0=sQuery(id+"F18.wireOp",EDGE,"E214");Q0=makeQuery(id+"F18.imprint","IMPRINT",FACE,{"disambiguationData":[TD([[makeQuery(id+"F18.imprint","IMPRINT",EDGE,{"derivedFrom":subQ0}),1.0]])]});}
            var Q1;
            {var subQ0=sQuery(id+"F18.wireOp",EDGE,"E215");Q1=makeQuery(id+"F18.imprint","IMPRINT",FACE,{"disambiguationData":[TD([[makeQuery(id+"F18.imprint","IMPRINT",EDGE,{"derivedFrom":subQ0}),1.0]])]});}
            extrude(context, id + "F19", {"entities" : qUnion([Q0, Q1]), "operationType" : NewBodyOperationType.REMOVE, "endBound" : BoundingType.THROUGH_ALL, "oppositeDirection" : true, "depth" : 25.4 * mm, "offsetDistance" : 25.4 * mm});
        }
    });
